# Revit family: WashBasin-Countertop-45cm-Bowl-Vitra-PluralSeries-7810
name_source: partatom
category: Plumbing Fixtures
revit_build: Autodesk Revit 2017 (Build: 20160225_1515(x64)
units: mm (PartAtom-declared; Revit-internal decimal feet)

## family parameters
Cut with Voids When Loaded = No
Host = Face
OmniClass Number = 23.45.05.14.14
OmniClass Title = Sinks/Lavatories
Part Type = Normal
Room Calculation Point = No
Round Connector Dimension = Use Diameter
Shared = Yes

## types (13) — shared parameters
BIMobject category = Sanitary - Basins
Brand = VitrA
CW Connection = No
Default Elevation = 850 mm
Description = VitrA Plural Countertop - 45cm - Bowl
Design country = Turkey
HW Connection = No
IFC Classification = Sanitary Terminal
Main Material = Ceramic
Manufacturer = VitrA
Manufacturer name = VitrA
Masterformat 2014 Code = 22 41 16
Masterformat 2014 Description = Residential Lavatories and Sinks
Mounting type = Countertop
NBS Referans Code = 35-65-70-94
NBS Referans Description = Wash Basin Systems
Nominal Depth (mm) = 382 mm
Nominal Height (mm) = 135 mm
Nominal Width (mm) = 453 mm  [stored 1.48622 ft]
OmniClass Code = 23.45.05.14.14
OmniClass Description = Sinks/Lavatories
Primary Material = <By Category>
Product certification = https://www.vitraglobal.com
Product family = Countertop WashBasin
Product group = Plural
UNSPSC Code = 301815
URL = https://www.vitraglobal.com
Uniclass 1.4 Code = L7212
Uniclass 1.4 Description = Washbasins
Uniclass 2.0 Code = SS-35-65-70-94
Uniclass 2.0 Description = Sanitary Dispensing And Disposal Units
Uniclass 2015 Code = Pr_40_20_96_81
Uniclass 2015 Name = Wash basins, Sinks and troughs
Uniformat II Code = D2010
Uniformat II Description = Plumbing Fixtures
Vent Connection = No
Warranty Period (Year) = 10 Years
Waste Connection = Yes
Youtube = https://www.youtube.com

## per-type parameters (varying)
| type | Article No. (default) | Color | Model | Product SKU | Product data url | Product url | Secondary Material | Technical description | Weight Net (kg) |
| WashBasin_Vitra_Plural_(Matt Terra Rossa)_7810B477-0016 | 7810B477-0016 | Matt Terra Rossa | 7810B477-0016 | 7810B477-0016 | https://www.vitraglobal.com |  | Matt Terra Rossa | https://www.vitraglobal.com | 6,55 |
| WashBasin_Vitra_Plural_(Matt Moss Green)_7810B475-0016 | 7810B475-0016 | Matt Moss Green | 7810B475-0016 | 7810B475-0016 | https://www.vitraglobal.com |  | Matt Moss Green | https://www.vitraglobal.com | 6,55 |
| WashBasin_Vitra_Plural_(MattClayBeige)_7810B474-0016 | 7810B474-0016 | Matt Clay Beige | 7810B474-0016 | 7810B474-0016 | https://www.vitraglobal.com |  | Matt Clay Beige | https://www.vitraglobal.com | 6,55 |
| WashBasin_Vitra_Plural_(MatteBlack)_7810B483-0016 | 7810B483-0016 | Matte Black | 7810B483-0016 | 7810B483-0016 | https://www.vitraglobal.com |  | MatteBlack | https://www.vitraglobal.com | 6,55 |
| WashBasin_Vitra_Plural_(MatteMink)_7810B450-0016 | 7810B450-0016 | Matte Mink | 7810B450-0016 | 7810B450-0016 | https://www.vitraglobal.com |  | MatteMink | https://www.vitraglobal.com | 6,55 |
| WashBasin_Vitra_Plural_(MatteBeige)_7810B420-0016 | 7810B420-0016 | Matte Beige | 7810B420-0016 | 7810B420-0016 | https://www.vitraglobal.com |  | MatteBeige | https://www.vitraglobal.com | 6,55 |
| WashBasin_Vitra_Plural_(MatteWhite)_7810B401-0016 | 7810B401-0016 | Matte White | 7810B401-0016 | 7810B401-0016 | https://www.vitraglobal.com |  | MatteWhite | https://www.vitraglobal.com | 6,55 |
| WashBasin_Vitra_Plural_(White)_7810B403-0016 | 7810B403-0016 | White | 7810B403-0016 | 7810B403-0016 | https://www.bimobject.com | https://www.vitraglobal.com | White | https://www.vitraglobal.com | 6.6 |
| WashBasin_Vitra_Plural_(White)_7810B403H0016 | 7810B403H0016 | White | 7810B403H0016 | 7810B403H0016 | https://www.bimobject.com | https://www.vitra-india.com | White | https://www.vitra-india.com | 6.6 |
| WashBasin_Vitra_Plural_(MatteWhite)_7810B401H0016 | 7810B401H0016 | Matte White | 7810B401H0016 | 7810B401H0016 |  | https://www.vitra-india.com | MatteWhite | https://www.vitra-india.com | 6,55 |
| WashBasin_Vitra_Plural_(MatteBeige)_7810B420H0016 | 7810B420H0016 | Matte Beige | 7810B420H0016 | 7810B420H0016 |  | https://www.vitra-india.com | MatteBeige | https://www.vitra-india.com | 6,55 |
| WashBasin_Vitra_Plural_(MatteMink)_7810B450H0016 | 7810B450H0016 | Matte Mink | 7810B450H0016 | 7810B450H0016 |  | https://www.vitra-india.com | MatteMink | https://www.vitra-india.com | 6,55 |
| WashBasin_Vitra_Plural_(MatteBlack)_7810B483H0016 | 7810B483H0016 | Matte Black | 7810B483H0016 | 7810B483H0016 |  | https://www.vitra-india.com | MatteBlack | https://www.vitra-india.com | 6,55 |

note: [stored X ft] marks values corroborated as IEEE doubles in the binary element streams (Revit-internal decimal feet)

## geometry (parser evidence)
native form markers: Sweep x2
no freeform markers — native parametric forms only
